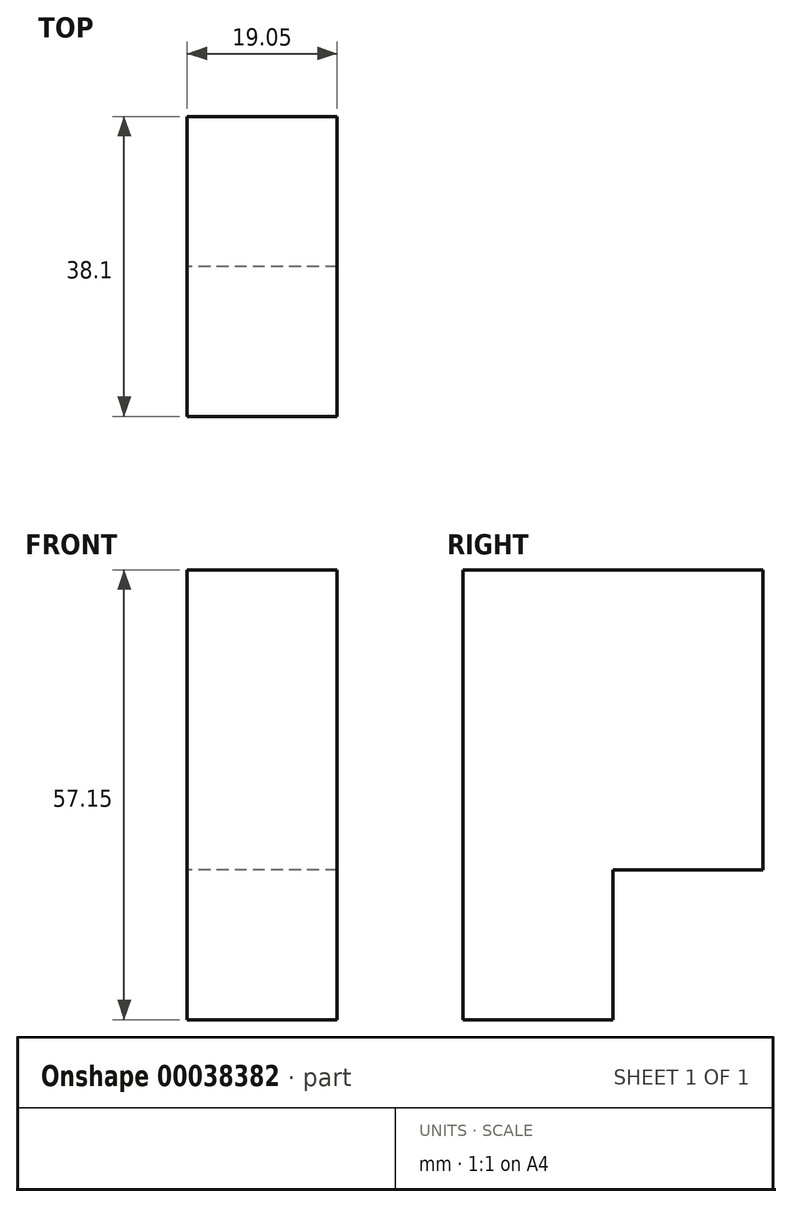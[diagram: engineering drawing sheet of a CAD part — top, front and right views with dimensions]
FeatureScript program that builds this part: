
annotation { "Feature Type Name" : "Feature", "Feature Type Description" : "" }
export const myFeature = defineFeature(function(context is Context, id is Id, definition is map)
    precondition{}
    {
        {
            var Q0;
            Q0=qCreatedBy(makeId("Top.planeOp"),FACE);
            var sketch = newSketch(context, id + "F0", { "sketchPlane" : qUnion([Q0])});
            skLineSegment(sketch, "E0.bottom", {"start": v(0, 0) * mm, "end": v(19.05, 0) * mm});
            skLineSegment(sketch, "E0.top", {"start": v(0, 19.05) * mm, "end": v(19.05, 19.05) * mm});
            skLineSegment(sketch, "E0.left", {"start": v(0, 0) * mm, "end": v(0, 19.05) * mm});
            skLineSegment(sketch, "E0.right", {"start": v(19.05, 0) * mm, "end": v(19.05, 19.05) * mm});
            skSolve(sketch);
        }
        {
            var Q0;
            Q0=makeQuery(id+"F0.imprint","IMPRINT",FACE,{"disambiguationData":[TD([[makeQuery(id+"F0.imprint","IMPRINT",EDGE,{"derivedFrom":sQuery(id+"F0.wireOp",EDGE,"E0.bottom")}),1.0]])]});
            extrude(context, id + "F1", {"entities" : qUnion([Q0]), "depth" : 19.05 * mm});
        }
        {
            var Q0;
            Q0=makeQuery(id+"F1.opExtrude","CAP_FACE",FACE,{"disambiguationData":[OSD([sQuery(id+"F0.wireOp",EDGE,"E0.bottom"),sQuery(id+"F0.wireOp",EDGE,"E0.top"),sQuery(id+"F0.wireOp",EDGE,"E0.left"),sQuery(id+"F0.wireOp",EDGE,"E0.right")])],"isStart":false});
            var sketch = newSketch(context, id + "F2", { "sketchPlane" : qUnion([Q0])});
            skSolve(sketch);
        }
        {
            var Q0;
            Q0=makeQuery(id+"F2.imprint","IMPRINT",FACE,{"disambiguationData":[TD([[makeQuery(id+"F2.imprint","IMPRINT",EDGE,{"derivedFrom":makeQuery(id+"F1.opExtrude","CAP_EDGE",EDGE,{"disambiguationData":[OSD([sQuery(id+"F0.wireOp",EDGE,"E0.bottom")])],"isStart":false})}),1.0]])]});
            extrude(context, id + "F3", {"entities" : qUnion([Q0]), "operationType" : NewBodyOperationType.ADD, "depth" : 19.05 * mm});
        }
        {
            var Q0;
            {var subQ0=sQuery(id+"F0.wireOp",EDGE,"E0.top");Q0=makeQuery(id+"F3.boolean.opBoolean","MERGE",FACE,{"derivedFrom":[makeQuery(id+"F1.opExtrude","SWEPT_FACE",FACE,{"disambiguationData":[OSD([subQ0])]}),makeQuery(id+"F3.opExtrude","SWEPT_FACE",FACE,{"disambiguationData":[OSD([subQ0])]})]});}
            var sketch = newSketch(context, id + "F4", { "sketchPlane" : qUnion([Q0])});
            skLineSegment(sketch, "E1.bottom", {"start": v(-19.05, 38.1) * mm, "end": v(0, 38.1) * mm});
            skLineSegment(sketch, "E1.top", {"start": v(-19.05, 19.05) * mm, "end": v(0, 19.05) * mm});
            skLineSegment(sketch, "E1.left", {"start": v(-19.05, 38.1) * mm, "end": v(-19.05, 19.05) * mm});
            skLineSegment(sketch, "E1.right", {"start": v(0, 38.1) * mm, "end": v(0, 19.05) * mm});
            skLineSegment(sketch, "E2.top", {"start": v(-19.05, 0) * mm, "end": v(0, 0) * mm});
            skLineSegment(sketch, "E2.left", {"start": v(-19.05, 19.05) * mm, "end": v(-19.05, 0) * mm});
            skLineSegment(sketch, "E2.right", {"start": v(0, 19.05) * mm, "end": v(0, 0) * mm});
            skSolve(sketch);
        }
        {
            var Q0;
            Q0=makeQuery(id+"F4.imprint","IMPRINT",FACE,{"disambiguationData":[TD([[makeQuery(id+"F4.imprint","IMPRINT",EDGE,{"derivedFrom":sQuery(id+"F4.wireOp",EDGE,"E1.bottom")}),1.0]])]});
            extrude(context, id + "F5", {"entities" : qUnion([Q0]), "operationType" : NewBodyOperationType.ADD, "depth" : 19.05 * mm});
        }
        {
            var Q0;
            Q0=makeQuery(id+"F5.boolean.opBoolean","MERGE",FACE,{"derivedFrom":[makeQuery(id+"F3.opExtrude","CAP_FACE",FACE,{"disambiguationData":[OSD([sQuery(id+"F0.wireOp",EDGE,"E0.bottom"),sQuery(id+"F0.wireOp",EDGE,"E0.top"),sQuery(id+"F0.wireOp",EDGE,"E0.left"),sQuery(id+"F0.wireOp",EDGE,"E0.right")])],"isStart":false}),makeQuery(id+"F5.opExtrude","SWEPT_FACE",FACE,{"disambiguationData":[OSD([sQuery(id+"F4.wireOp",EDGE,"E1.bottom")])]})]});
            var sketch = newSketch(context, id + "F6", { "sketchPlane" : qUnion([Q0])});
            skLineSegment(sketch, "E3.bottom", {"start": v(19.05, 0) * mm, "end": v(0, 0) * mm});
            skLineSegment(sketch, "E3.top", {"start": v(19.05, 19.05) * mm, "end": v(0, 19.05) * mm});
            skLineSegment(sketch, "E3.left", {"start": v(19.05, 0) * mm, "end": v(19.05, 19.05) * mm});
            skLineSegment(sketch, "E3.right", {"start": v(0, 0) * mm, "end": v(0, 19.05) * mm});
            skLineSegment(sketch, "E4.top", {"start": v(19.05, 38.1) * mm, "end": v(0, 38.1) * mm});
            skLineSegment(sketch, "E4.left", {"start": v(19.05, 19.05) * mm, "end": v(19.05, 38.1) * mm});
            skLineSegment(sketch, "E4.right", {"start": v(0, 19.05) * mm, "end": v(0, 38.1) * mm});
            skSolve(sketch);
        }
        {
            var Q0;
            Q0=makeQuery(id+"F6.imprint","IMPRINT",FACE,{"disambiguationData":[TD([[makeQuery(id+"F6.imprint","IMPRINT",EDGE,{"derivedFrom":sQuery(id+"F6.wireOp",EDGE,"E3.bottom")}),1.0]])]});
            extrude(context, id + "F7", {"entities" : qUnion([Q0]), "operationType" : NewBodyOperationType.ADD, "depth" : 19.05 * mm});
        }
        {
            var Q0;
            Q0=makeQuery(id+"F7.opExtrude","SWEPT_FACE",FACE,{"disambiguationData":[OSD([sQuery(id+"F6.wireOp",EDGE,"E3.top")])]});
            extrude(context, id + "F8", {"entities" : qUnion([Q0]), "operationType" : NewBodyOperationType.ADD, "depth" : 19.05 * mm});
        }
    });
